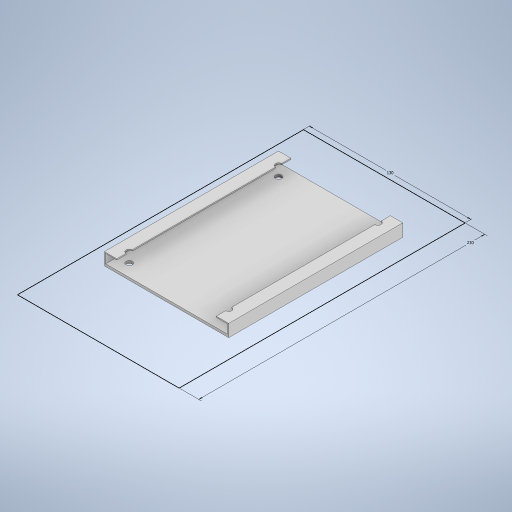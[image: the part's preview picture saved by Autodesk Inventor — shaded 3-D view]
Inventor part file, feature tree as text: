
AUTODESK INVENTOR PART (.ipt)
format: ipt  version: 2024 (Build 280153000, 153)  size: 433,152 bytes
history: native  units: mm
features: sketch x13, extrude x13, other x1
ambient origin geometry x8: Origin, YZ Plane, XZ Plane, XY Plane, X Axis, Y Axis, Z Axis, Center Point
bodies: Body1 (feature_tree)
feature tree (27):
  other  "Sólido1"
  sketch  "Boceto1"  dims[d0=130.0mm d1=230.0mm]
  extrude  "Extrusión1"  Depth=230.0mm
  extrude  "Extrusión2"  Depth=3.0mm
  extrude  "Extrusión3"  Depth=1.0mm
  extrude  "Extrusión4"  Depth=10.0mm
  extrude  "Extrusión5"  Depth=10.0mm TaperAngle=0.0deg
  extrude  "Extrusión6"  TaperAngle=0.0deg  [1 undecoded]
  extrude  "Extrusión7"  Depth=211.5mm TaperAngle=0.0deg
  extrude  "Extrusión8"  Depth=3.0mm
  extrude  "Extrusión9"  Depth=3.0mm
  extrude  "Extrusión10"  Depth=10.0mm
  extrude  "Extrusión11"  Depth=10.0mm
  extrude  "Extrusión12"  Depth=10.0mm
  extrude  "Extrusión13"  Depth=10.0mm
  sketch  "Boceto2"  dims[d2=3.0mm d3=0.0mm d4=3.0mm]
  sketch  "Boceto3"  dims[d5=60.0mm d6=0.0mm d7=1.0mm]
  sketch  "Boceto4"  dims[d8=10.0mm d9=0.0mm d10=10.0mm]
  sketch  "Boceto5"  dims[d11=10.0mm d12=115.25mm d13=0.0mm]
  sketch  "Boceto6"  dims[d14=10.0mm d15=0.0mm]
  sketch  "Boceto7"  dims[d16=0.0mm d17=211.5mm d18=0.0mm]
  sketch  "Boceto8"  dims[d19=3.0mm d20=3.0mm]
  sketch  "Boceto9"  dims[d21=3.0mm d22=3.0mm]
  sketch  "Boceto11"  dims[d23=10.0mm d24=10.0mm]
  sketch  "Boceto12"  dims[d25=10.0mm d26=10.0mm]
  sketch  "Boceto13"  dims[d27=10.0mm d28=10.0mm]
  sketch  "Boceto14"  dims[d29=10.0mm d30=10.0mm d31=211.5mm d32=0.0mm d33=8.0mm d34=8.0mm d35=8.0mm d36=8.0mm d37=25.0mm d38=25.0mm d39=25.0mm d40=25.0mm d41=25.0mm d42=25.0mm d43=25.0mm d44=25.0mm d45=10.0mm d46=0.0mm d47=70.0mm d48=10.0mm d49=35.0mm d50=30.0mm d51=30.0mm d52=5.0mm d53=5.0mm d54=5.0mm d55=5.0mm d56=5.0mm d57=5.0mm d58=10.0mm d59=0.0mm d60=90.0mm d61=130.0mm d62=20.0mm d63=20.0mm d64=60.0mm d65=5.0mm d66=5.0mm d67=5.0mm d68=5.0mm d69=5.0mm d70=5.0mm d71=5.0mm d72=5.0mm d73=5.0mm d74=5.0mm d75=5.0mm d76=5.0mm d77=10.0mm d78=0.0mm d79=61.0mm d80=0.0mm d81=10.0mm d82=61.0mm d83=0.0mm d84=1.0mm d85=1.0mm d86=0.0mm d87=10.0mm d88=10.0mm d89=100.0mm d90=10.0mm d91=10.0mm d92=140.0mm d93=0.0mm d94=140.0mm d95=0.0mm]
note: 1 required parameter value undecoded (feature->parameter linkage not recoverable at this tier; creation-order binding heuristic only, values carry confidence <= 0.55)
